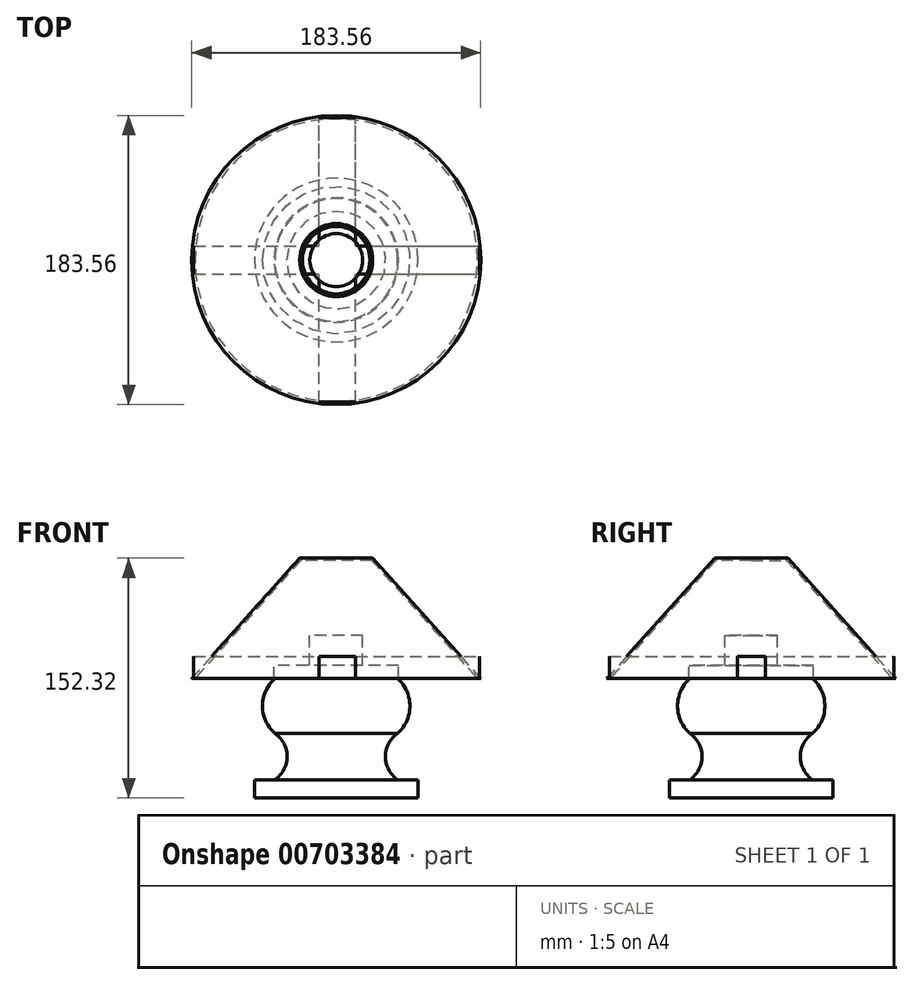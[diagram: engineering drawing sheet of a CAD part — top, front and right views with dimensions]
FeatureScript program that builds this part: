
annotation { "Feature Type Name" : "Feature", "Feature Type Description" : "" }
export const myFeature = defineFeature(function(context is Context, id is Id, definition is map)
    precondition{}
    {
        {
            var Q0;
            Q0=qCreatedBy(makeId("Front.planeOp"),FACE);
            var sketch = newSketch(context, id + "F0", { "sketchPlane" : qUnion([Q0])});
            skLineSegment(sketch, "E0", {"start": v(-23.18, 76.57) * mm, "end": v(-91.78, 0) * mm});
            skLineSegment(sketch, "E1", {"start": v(-91.78, 0) * mm, "end": v(-38.98, 0) * mm});
            skArc(sketch, "E2", {"start": v(-38.98, 0) * mm, "mid": v(-46.8, -17.37) * mm, "end": v(-38.98, -34.74) * mm});
            skArc(sketch, "E3", {"start": v(-38.98, -64.2) * mm, "mid": v(-31.18, -49.47) * mm, "end": v(-38.98, -34.74) * mm});
            skLineSegment(sketch, "E4.bottom", {"start": v(-51.96, -64.2) * mm, "end": v(0, -64.2) * mm});
            skLineSegment(sketch, "E4.top", {"start": v(-51.96, -75.75) * mm, "end": v(0, -75.75) * mm});
            skLineSegment(sketch, "E4.left", {"start": v(-51.96, -64.2) * mm, "end": v(-51.96, -75.75) * mm});
            skLineSegment(sketch, "E4.right", {"start": v(0, -64.2) * mm, "end": v(0, -75.75) * mm});
            skLineSegment(sketch, "E5", {"start": v(0, -64.2) * mm, "end": v(0, 76.57) * mm});
            skLineSegment(sketch, "E6", {"start": v(0, 76.57) * mm, "end": v(-23.18, 76.57) * mm});
            skSolve(sketch);
        }
        {
            var Q0;
            Q0 = qSketchRegion(id + "F0", true);
            var Q1;
            Q1=sQuery(id+"F0.wireOp",EDGE,"E5");
            revolve(context, id + "F1", {"surfaceOperationType" : NewSurfaceOperationType.NEW, "entities" : qUnion([Q0]), "axis" : qUnion([Q1]), "revolveType" : RevolveType.FULL});
        }
        {
            var Q0;
            Q0=qCreatedBy(makeId("Front.planeOp"),FACE);
            var sketch = newSketch(context, id + "F2", { "sketchPlane" : qUnion([Q0])});
            skLineSegment(sketch, "E7", {"start": v(-22.5, 75.19) * mm, "end": v(-91.57, -2.09) * mm});
            skLineSegment(sketch, "E8", {"start": v(-91.57, -2.09) * mm, "end": v(-43.48, -2.09) * mm});
            skLineSegment(sketch, "E9", {"start": v(-43.48, -2.09) * mm, "end": v(-39.52, 0) * mm});
            skLineSegment(sketch, "E10", {"start": v(-39.52, 0) * mm, "end": v(-39.52, 8.47) * mm});
            skLineSegment(sketch, "E11", {"start": v(-39.52, 8.47) * mm, "end": v(-16.79, 8.47) * mm});
            skLineSegment(sketch, "E12", {"start": v(-16.79, 8.47) * mm, "end": v(-16.79, 27.39) * mm});
            skLineSegment(sketch, "E13", {"start": v(-16.79, 27.39) * mm, "end": v(0, 27.39) * mm});
            skLineSegment(sketch, "E14", {"start": v(0, 27.39) * mm, "end": v(0, 79.44) * mm});
            skLineSegment(sketch, "E15", {"start": v(-22.5, 75.19) * mm, "end": v(-19.94, 78.4) * mm});
            skLineSegment(sketch, "E16", {"start": v(-19.94, 78.4) * mm, "end": v(0, 79.44) * mm});
            skSolve(sketch);
        }
        {
            var Q0;
            Q0 = qSketchRegion(id + "F2", true);
            var Q1;
            Q1=sQuery(id+"F2.wireOp",EDGE,"E14");
            revolve(context, id + "F3", {"operationType" : NewBodyOperationType.REMOVE, "surfaceOperationType" : NewSurfaceOperationType.NEW, "entities" : qUnion([Q0]), "axis" : qUnion([Q1]), "revolveType" : RevolveType.FULL, "oppositeDirection" : true});
        }
        {
            var Q0;
            Q0=qCreatedBy(makeId("Top.planeOp"),FACE);
            var sketch = newSketch(context, id + "F4", { "sketchPlane" : qUnion([Q0])});
            skLineSegment(sketch, "E17.bottom", {"start": v(-90.5, -8.74) * mm, "end": v(90.98, -8.74) * mm});
            skLineSegment(sketch, "E17.top", {"start": v(-90.5, 8.92) * mm, "end": v(90.98, 8.92) * mm});
            skLineSegment(sketch, "E17.left", {"start": v(-90.5, -8.74) * mm, "end": v(-90.5, 8.92) * mm});
            skLineSegment(sketch, "E17.right", {"start": v(90.98, -8.74) * mm, "end": v(90.98, 8.92) * mm});
            skLineSegment(sketch, "E18.bottom", {"start": v(-10.82, -90.18) * mm, "end": v(12.25, -90.18) * mm});
            skLineSegment(sketch, "E18.top", {"start": v(-10.82, 90.5) * mm, "end": v(12.25, 90.5) * mm});
            skLineSegment(sketch, "E18.left", {"start": v(-10.82, -90.18) * mm, "end": v(-10.82, 90.5) * mm});
            skLineSegment(sketch, "E18.right", {"start": v(12.25, -90.18) * mm, "end": v(12.25, 90.5) * mm});
            skSolve(sketch);
        }
        {
            var Q0;
            Q0 = qSketchRegion(id + "F4", true);
            extrude(context, id + "F5", {"entities" : qUnion([Q0]), "depth" : 14.12 * mm, "offsetDistance" : 25.4 * mm});
        }
    });
